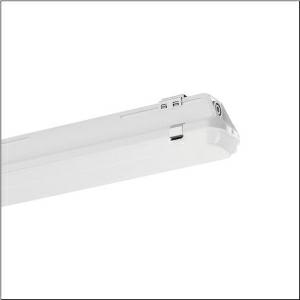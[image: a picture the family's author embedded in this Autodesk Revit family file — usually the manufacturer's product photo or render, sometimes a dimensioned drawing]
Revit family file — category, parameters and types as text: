
# Revit family: monsun_r__11_51fp107p4b0u_d884
name_source: partatom
category: Lighting Fixtures
units: mm (PartAtom-declared; Revit-internal decimal feet)

## family parameters
Cut with Voids When Loaded = No
Host = Face
Light Source = No
Part Type = Normal
Room Calculation Point = No
Round Connector Dimension = Use Diameter
Shared = No

## types (1)
- Monsun® 11 (1 x LED, 12070 lm, 62.4 W, 4000K)
    Apparent Load = 62 VA
    CIE Flux Codes = 47 76 93 94 100
    Color Rendering = 80
    Color Temperature = 4000K
    Default Elevation = 1800 mm
    Description = Monsun® 11, damp-proof luminaire, chain hanger, primary optical cover: enclosure, of PMMA, light emission: direct distribution, primary light characteristic: symmetric, installation type: suspended mounting, surface-mounted, horizontal mounting, vertical mounting, LED, rated luminous flux: 12.070lm, luminous efficacy: 193lm/W, light colour: 840, colour temperature: 4000K, control gear: ON/OFF, with terminal, 3-pole, max. 2.5mm², mains connection: 220..240V, AC, 50/60Hz, rated input power: 62W, luminaire housing, of glass-fibre reinforced polyester, uncoated, bright grey, incl. chain hanger, length: 1.590mm, width: 90mm, height: 88mm, clip for enclosure, of stainless steel (V2A), ceiling mounting element, of stainless steel (V2A), chain hanger, of stainless steel (V2A), protection rating (complete): IP66, insulation class (complete): insulation class I (protective earthing), certification: CE, ENEC, VDE, UKCA, protection symbol: D, impact resistance: IK04, permissible operating ambient temperature: -35..+35°C, standard: EN 50419, EN 60598-2-1, contact your sales advisor before using the luminaires in applications with unclear chemical exposure, large temperature fluctuations or condensation-forming humidity, LABS conformity tested according to VDMA 24364:2018-05, no direct snow, no direct sun, no direct rain, for indoor or canopied outdoor use, corresponds to IFS (International Featured Standards) requirements for safety and quality in the food industry, packaging unit: 1 piece
    Height = 89 mm
    Lamp = 1 x LED
    Lamp Light Flux = 12070 lm
    Lamp Power = 62.4 W
    Lamp count = 1
    Length = 1590 mm
    Luminous efficacy = 193 lm/W
    Manufacturer = Siteco
    ModVariant = No
    Model = 51FP107P4B0U
    Mounting Place = Ceiling
    Mounting Type = Surface mounted
    Number of Poles = 1
    OnlyDefault = Yes
    Power Factor = 1
    Product Name = Monsun® 11
    Product group = damp-proof luminaire
    ProductGroupID = 301
    Protection Class = Protection class I
    Protection Degree = IP 66
    RLX_Detail_Level = 1
    RLX_Emergency_Light_Flux = 0 lm
    RLX_Emergency_Type = 0
    RLX_Emergency_Type_DB = No
    RlxData = <blob elided: 88381 chars, md5=872548ff>
    Socket = socket
    Standby Power = 0 W
    System Light Flux = 12070 lm
    System Power = 62 W
    Type Comments = Product without accessories
    Type Image = l_1349237.jpg
    URL = http://relux.com
    VarID = ---
    Voltage = 0 V
    Weight = 0.00 kg
    Width = 90 mm

## geometry (parser evidence)
native form markers: Blend x4, Sweep x14
no freeform markers — native parametric forms only
